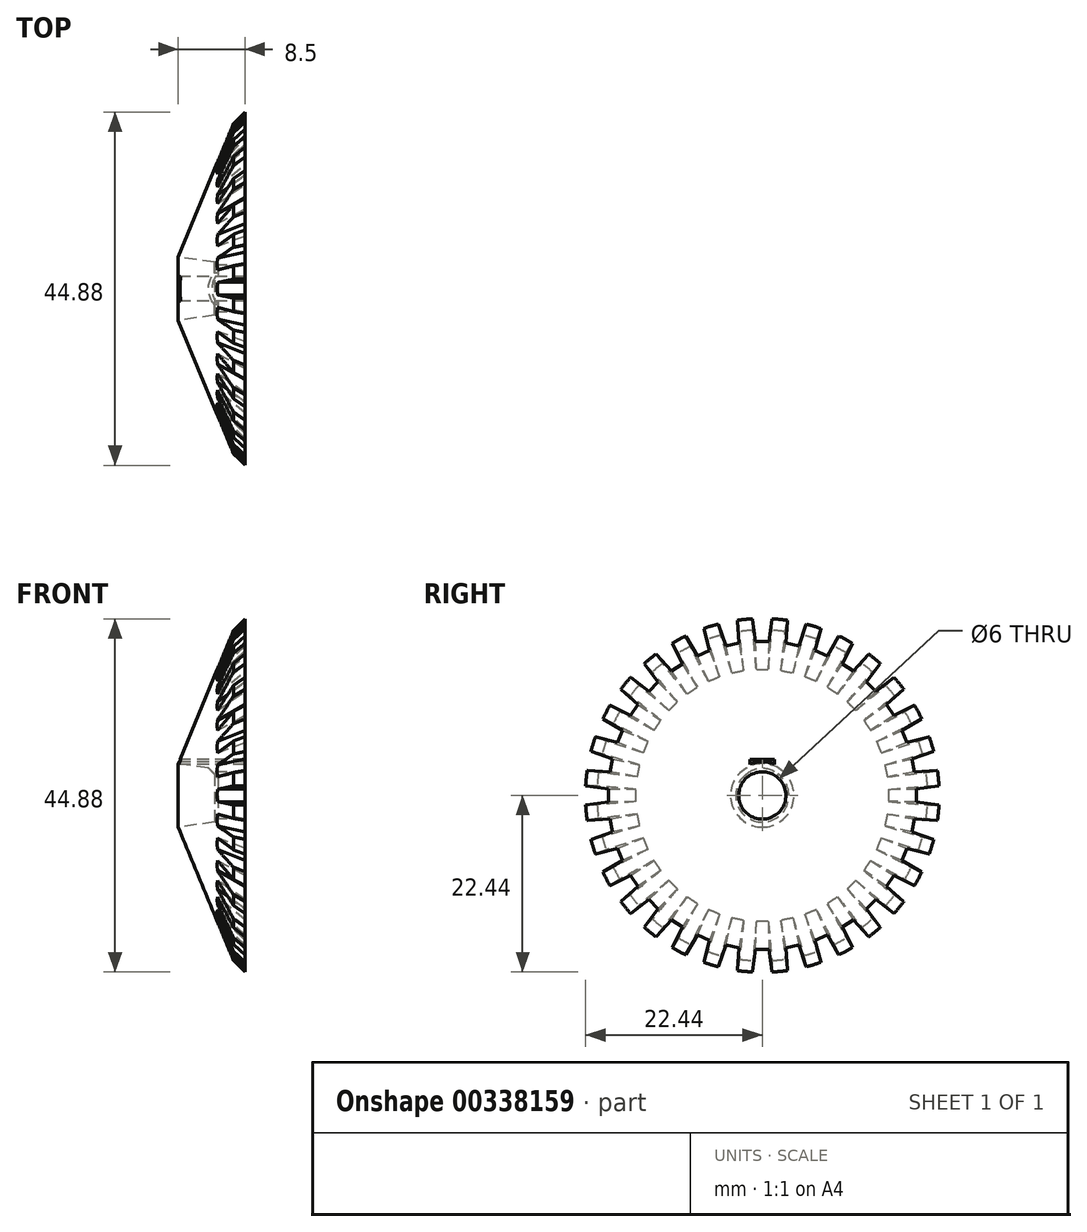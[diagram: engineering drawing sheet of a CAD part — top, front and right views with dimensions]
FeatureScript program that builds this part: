
annotation { "Feature Type Name" : "Feature", "Feature Type Description" : "" }
export const myFeature = defineFeature(function(context is Context, id is Id, definition is map)
    precondition{}
    {
        {
            var Q0;
            Q0=qCreatedBy(makeId("Front.planeOp"),FACE);
            var sketch = newSketch(context, id + "F0", { "sketchPlane" : qUnion([Q0])});
            skLineSegment(sketch, "E0", {"start": v(0, 0) * mm, "end": v(35.34, 35.34) * mm});
            skLineSegment(sketch, "E1", {"start": v(0, 0) * mm, "end": v(38.3, 0) * mm});
            skLineSegment(sketch, "E2", {"start": v(0, 0) * mm, "end": v(-10.6, 10.6) * mm});
            skLineSegment(sketch, "E3", {"start": v(-10.6, 10.6) * mm, "end": v(24.73, 45.94) * mm});
            skLineSegment(sketch, "E4", {"start": v(24.73, 45.94) * mm, "end": v(35.34, 35.34) * mm});
            skSolve(sketch);
        }
        {
            var Q0;
            Q0=makeQuery(id+"F0.imprint","IMPRINT",FACE,{"disambiguationData":[TD([[makeQuery(id+"F0.imprint","IMPRINT",EDGE,{"derivedFrom":sQuery(id+"F0.wireOp",EDGE,"E0")}),1.0]])]});
            extrude(context, id + "F1", {"entities" : qUnion([Q0]), "endBound" : BoundingType.SYMMETRIC, "depth" : 4 * mm});
        }
        {
            var Q0;
            Q0=makeQuery(id+"F1.opExtrude","SWEPT_FACE",FACE,{"disambiguationData":[OSD([sQuery(id+"F0.wireOp",EDGE,"E3")])]});
            var sketch = newSketch(context, id + "F2", { "sketchPlane" : qUnion([Q0])});
            skPoint(sketch, "E5", {"position": v(-2, 49.97) * mm});
            skPoint(sketch, "E6", {"position": v(-1, -0.02) * mm});
            skLineSegment(sketch, "E7", {"start": v(-1, -0.02) * mm, "end": v(1, 0.02) * mm, "construction": true});
            skPoint(sketch, "E8", {"position": v(0, 0) * mm});
            skLineSegment(sketch, "E9", {"start": v(0, -8) * mm, "end": v(0, -12.28) * mm, "construction": true});
            skLineSegment(sketch, "E10", {"start": v(1.74, 52.97) * mm, "end": v(-1.74, 52.97) * mm});
            skLineSegment(sketch, "E11", {"start": v(0.94, -3.02) * mm, "end": v(-0.94, -3.02) * mm});
            skLineSegment(sketch, "E12", {"start": v(-0.94, -3.02) * mm, "end": v(-1.74, 52.97) * mm});
            skLineSegment(sketch, "E13.MirrorCS", {"start": v(0.94, -3.02) * mm, "end": v(1.74, 52.97) * mm});
            skSolve(sketch);
        }
        {
            var Q0;
            Q0=qCreatedBy(makeId("Top.planeOp"),FACE);
            var sketch = newSketch(context, id + "F3", { "sketchPlane" : qUnion([Q0])});
            skLineSegment(sketch, "E14", {"start": v(0, 0) * mm, "end": v(0, -17.72) * mm});
            skLineSegment(sketch, "E15", {"start": v(0, 0) * mm, "end": v(21.3, 0) * mm});
            skSolve(sketch);
        }
        {
            var Q0;
            Q0=makeQuery(id+"F1.opExtrude","CAP_FACE",FACE,{"disambiguationData":[OSD([sQuery(id+"F0.wireOp",EDGE,"E0"),sQuery(id+"F0.wireOp",EDGE,"E2"),sQuery(id+"F0.wireOp",EDGE,"E3"),sQuery(id+"F0.wireOp",EDGE,"E4")])],"isStart":false});
            var Q1;
            Q1=sQuery(id+"F3.wireOp",EDGE,"E15");
            revolve(context, id + "F4", {"operationType" : NewBodyOperationType.ADD, "entities" : qUnion([Q0]), "axis" : qUnion([Q1]), "revolveType" : RevolveType.FULL});
        }
        {
            var Q0;
            {var subQ0=sQuery(id+"F2.wireOp",EDGE,"E12");var subQ1=sQuery(id+"F0.wireOp",EDGE,"E3");var subQ2=makeQuery(id+"F1.opExtrude","SWEPT_EDGE",EDGE,{"disambiguationData":[OSD([sQuery(id+"F0.wireOp",EDGE,"E2"),subQ1])]});var subQ3=makeQuery(id+"F2.imprint","INTERSECT",VERTEX,{"derivedFrom":[subQ2,subQ0]});Q0=makeQuery(id+"F2.imprint","IMPRINT",FACE,{"disambiguationData":[TD([[makeQuery(id+"F2.imprint","IMPRINT",EDGE,{"disambiguationData":[TD([[subQ3,-1.0]])],"derivedFrom":subQ0}),-1.0]])]});}
            var Q1;
            {var subQ0=sQuery(id+"F2.wireOp",EDGE,"E11");Q1=makeQuery(id+"F2.imprint","IMPRINT",FACE,{"disambiguationData":[TD([[makeQuery(id+"F2.imprint","IMPRINT",EDGE,{"derivedFrom":subQ0}),-1.0]])]});}
            var Q2;
            {var subQ0=sQuery(id+"F2.wireOp",EDGE,"E10");Q2=makeQuery(id+"F2.imprint","IMPRINT",FACE,{"disambiguationData":[TD([[makeQuery(id+"F2.imprint","IMPRINT",EDGE,{"derivedFrom":subQ0}),1.0]])]});}
            extrude(context, id + "F5", {"entities" : qUnion([Q0, Q1, Q2]), "oppositeDirection" : true, "depth" : 2 * mm, "hasDraft" : true, "draftAngle" : 10 * degree, "draftPullDirection" : true, "hasSecondDirection" : true, "secondDirectionOppositeDirection" : false, "secondDirectionDepth" : 1 * mm});
        }
        {
            var Q0;
            Q0=makeQuery(id+"F5.opExtrude","SWEPT_BODY",BODY,{"disambiguationData":[OSD([sQuery(id+"F2.wireOp",EDGE,"E10"),sQuery(id+"F2.wireOp",EDGE,"E11"),sQuery(id+"F2.wireOp",EDGE,"E12"),sQuery(id+"F2.wireOp",EDGE,"E13.MirrorCS")])]});
            var Q1;
            Q1=sQuery(id+"F3.wireOp",EDGE,"E15");
            circularPattern(context, id + "F6", {"operationType" : NewBodyOperationType.REMOVE, "entities" : qUnion([Q0]), "axis" : qUnion([Q1]), "angle" : 360 * degree, "instanceCount" : 32, "equalSpace" : true});
        }
        {
            var Q0;
            Q0=qCreatedBy(makeId("Right.planeOp"),FACE);
            var sketch = newSketch(context, id + "F7", { "sketchPlane" : qUnion([Q0])});
            skCircle(sketch, "E16", {"center": v(0, 0) * mm, "radius": 35.4 * mm});
            skPoint(sketch, "E17", {"position": v(0, 45.94) * mm});
            skCircle(sketch, "E18", {"center": v(0, 0) * mm, "radius": 3 * mm});
            skSolve(sketch);
        }
        {
            var Q0;
            Q0=makeQuery(id+"F7.imprint","IMPRINT",FACE,{"disambiguationData":[TD([[makeQuery(id+"F7.imprint","IMPRINT",EDGE,{"derivedFrom":sQuery(id+"F7.wireOp",EDGE,"E16")}),1.0]])]});
            var Q1;
            Q1=sQuery(id+"F0.wireOp",VERTEX,"E4.end");
            extrude(context, id + "F8", {"entities" : qUnion([Q0]), "operationType" : NewBodyOperationType.ADD, "endBound" : BoundingType.UP_TO_VERTEX, "endBoundEntityVertex" : qUnion([Q1]), "depth" : 56.9 * mm, "hasSecondDirection" : true, "secondDirectionOppositeDirection" : false, "secondDirectionDepth" : 25.7 * mm});
        }
        {
            var Q0;
            Q0=qCreatedBy(makeId("Top.planeOp"),FACE);
            var sketch = newSketch(context, id + "F9", { "sketchPlane" : qUnion([Q0])});
            skLineSegment(sketch, "E19.bottom", {"start": v(26.17, 74.13) * mm, "end": v(56.17, 74.13) * mm});
            skLineSegment(sketch, "E19.top", {"start": v(26.17, -66.7) * mm, "end": v(56.17, -66.7) * mm});
            skLineSegment(sketch, "E19.left", {"start": v(26.17, 74.13) * mm, "end": v(26.17, -66.7) * mm});
            skLineSegment(sketch, "E19.right", {"start": v(56.17, 74.13) * mm, "end": v(56.17, -66.7) * mm});
            skSolve(sketch);
        }
        {
            var Q0;
            Q0=makeQuery(id+"F9.imprint","IMPRINT",FACE,{"disambiguationData":[TD([[makeQuery(id+"F9.imprint","IMPRINT",EDGE,{"derivedFrom":sQuery(id+"F9.wireOp",EDGE,"E19.bottom")}),-1.0]])]});
            extrude(context, id + "F10", {"entities" : qUnion([Q0]), "operationType" : NewBodyOperationType.REMOVE, "endBound" : BoundingType.SYMMETRIC, "oppositeDirection" : true, "depth" : 112 * mm});
        }
        {
            var Q0;
            Q0=qCreatedBy(makeId("Right.planeOp"),FACE);
            var sketch = newSketch(context, id + "F11", { "sketchPlane" : qUnion([Q0])});
            skCircle(sketch, "E20", {"center": v(0, 0) * mm, "radius": 10.6 * mm});
            skPoint(sketch, "E21", {"position": v(0, 10.6) * mm});
            skCircle(sketch, "E22", {"center": v(0, 0) * mm, "radius": 3 * mm});
            skLineSegment(sketch, "E23.bottom", {"start": v(1.56, 2.56) * mm, "end": v(-1.56, 2.56) * mm, "construction": true});
            skLineSegment(sketch, "E23.top", {"start": v(1.56, -1.18) * mm, "end": v(-1.56, -1.18) * mm});
            skLineSegment(sketch, "E23.left", {"start": v(1.56, 2.56) * mm, "end": v(1.56, -1.18) * mm});
            skLineSegment(sketch, "E23.right", {"start": v(-1.56, 2.56) * mm, "end": v(-1.56, -1.18) * mm});
            skPoint(sketch, "E24", {"position": v(0, 2.56) * mm});
            skLineSegment(sketch, "E25.top", {"start": v(1.56, 4.56) * mm, "end": v(-1.56, 4.56) * mm});
            skLineSegment(sketch, "E25.left", {"start": v(1.56, -1.18) * mm, "end": v(1.56, 4.56) * mm});
            skLineSegment(sketch, "E25.right", {"start": v(-1.56, -1.18) * mm, "end": v(-1.56, 4.56) * mm});
            skSolve(sketch);
        }
        {
            var Q0;
            Q0=makeQuery(id+"F11.imprint","IMPRINT",FACE,{"disambiguationData":[TD([[makeQuery(id+"F11.imprint","IMPRINT",EDGE,{"derivedFrom":sQuery(id+"F11.wireOp",EDGE,"E20")}),1.0]])]});
            var Q1;
            {var subQ5=sQuery(id+"F11.wireOp",EDGE,"E23.top");Q1=makeQuery(id+"F11.imprint","IMPRINT",FACE,{"disambiguationData":[TD([[makeQuery(id+"F11.imprint","IMPRINT",EDGE,{"derivedFrom":subQ5}),1.0]])]});}
            var Q2;
            {var subQ5=sQuery(id+"F11.wireOp",EDGE,"E23.top");Q2=makeQuery(id+"F11.imprint","IMPRINT",FACE,{"disambiguationData":[TD([[makeQuery(id+"F11.imprint","IMPRINT",EDGE,{"derivedFrom":subQ5}),-1.0]])]});}
            var Q3;
            {var subQ5=sQuery(id+"F11.wireOp",EDGE,"E25.top");Q3=makeQuery(id+"F11.imprint","IMPRINT",FACE,{"disambiguationData":[TD([[makeQuery(id+"F11.imprint","IMPRINT",EDGE,{"derivedFrom":subQ5}),1.0]])]});}
            extrude(context, id + "F12", {"entities" : qUnion([Q0, Q1, Q2, Q3]), "operationType" : NewBodyOperationType.ADD, "oppositeDirection" : true, "depth" : 9 * mm, "hasDraft" : true, "draftAngle" : 8 * degree, "draftPullDirection" : true});
        }
        {
            var Q0;
            Q0=makeQuery(id+"F12.opExtrude","CAP_FACE",FACE,{"disambiguationData":[OSD([sQuery(id+"F11.wireOp",EDGE,"E20")])],"isStart":false});
            var sketch = newSketch(context, id + "F13", { "sketchPlane" : qUnion([Q0])});
            skCircle(sketch, "E26", {"center": v(0, 0) * mm, "radius": 3 * mm});
            skLineSegment(sketch, "E27.bottom", {"start": v(-1.56, 4.56) * mm, "end": v(1.56, 4.56) * mm});
            skLineSegment(sketch, "E27.top", {"start": v(-1.56, 2) * mm, "end": v(1.56, 2) * mm, "construction": true});
            skLineSegment(sketch, "E27.left", {"start": v(-1.56, 4.56) * mm, "end": v(-1.56, 2) * mm});
            skLineSegment(sketch, "E27.right", {"start": v(1.56, 4.56) * mm, "end": v(1.56, 2) * mm});
            skSolve(sketch);
        }
        {
            var Q0;
            Q0=makeQuery(id+"F10.boolean.opBoolean","COPY",FACE,{"derivedFrom":makeQuery(id+"F10.opExtrude","SWEPT_FACE",FACE,{"disambiguationData":[OSD([sQuery(id+"F9.wireOp",EDGE,"E19.left")])]})});
            var sketch = newSketch(context, id + "F14", { "sketchPlane" : qUnion([Q0])});
            skCircle(sketch, "E28", {"center": v(0, 0) * mm, "radius": 3 * mm});
            skSolve(sketch);
        }
        {
            var Q0;
            Q0=makeQuery(id+"F14.imprint","IMPRINT",FACE,{"disambiguationData":[TD([[makeQuery(id+"F14.imprint","IMPRINT",EDGE,{"derivedFrom":sQuery(id+"F14.wireOp",EDGE,"E28")}),-1.0]])]});
            var Q1;
            Q1=sQuery(id+"F11.wireOp",VERTEX,"E21");
            extrude(context, id + "F15", {"entities" : qUnion([Q0]), "operationType" : NewBodyOperationType.ADD, "endBound" : BoundingType.UP_TO_VERTEX, "oppositeDirection" : true, "endBoundEntityVertex" : qUnion([Q1]), "depth" : 25 * mm, "hasDraft" : true, "draftAngle" : 3 * degree});
        }
        {
            var Q0;
            {var subQ5=sQuery(id+"F13.wireOp",EDGE,"E27.bottom");Q0=makeQuery(id+"F13.imprint","IMPRINT",FACE,{"disambiguationData":[TD([[makeQuery(id+"F13.imprint","IMPRINT",EDGE,{"derivedFrom":subQ5}),-1.0]])]});}
            var Q1;
            {var subQ0=sQuery(id+"F13.wireOp",EDGE,"E26");var subQ1=makeQuery(id+"F13.imprint","INTERSECT",VERTEX,{"derivedFrom":[subQ0,sQuery(id+"F13.wireOp",EDGE,"E27.left")]});Q1=makeQuery(id+"F13.imprint","IMPRINT",FACE,{"disambiguationData":[TD([[makeQuery(id+"F13.imprint","IMPRINT",EDGE,{"disambiguationData":[TD([[subQ1,1.0]])],"derivedFrom":subQ0}),1.0]])]});}
            extrude(context, id + "F16", {"entities" : qUnion([Q0, Q1]), "operationType" : NewBodyOperationType.REMOVE, "oppositeDirection" : true, "depth" : 288.6 * mm});
        }
        {
            var Q0;
            Q0=makeQuery(id+"F15.boolean.opBoolean","MERGE",FACE,{"derivedFrom":[makeQuery(id+"F10.boolean.opBoolean","COPY",FACE,{"derivedFrom":makeQuery(id+"F10.opExtrude","SWEPT_FACE",FACE,{"disambiguationData":[OSD([sQuery(id+"F9.wireOp",EDGE,"E19.left")])]})}),makeQuery(id+"F15.opExtrude","CAP_FACE",FACE,{"disambiguationData":[OSD([sQuery(id+"F14.wireOp",EDGE,"E28")])],"isStart":true})]});
            var sketch = newSketch(context, id + "F17", { "sketchPlane" : qUnion([Q0])});
            skLineSegment(sketch, "E29.bottom", {"start": v(-85.01, 76.56) * mm, "end": v(100.06, 76.56) * mm});
            skLineSegment(sketch, "E29.top", {"start": v(-85.01, -83.72) * mm, "end": v(100.06, -83.72) * mm});
            skLineSegment(sketch, "E29.left", {"start": v(-85.01, 76.56) * mm, "end": v(-85.01, -83.72) * mm});
            skLineSegment(sketch, "E29.right", {"start": v(100.06, 76.56) * mm, "end": v(100.06, -83.72) * mm});
            skSolve(sketch);
        }
        {
            var Q0;
            Q0=makeQuery(id+"F17.imprint","IMPRINT",FACE,{"disambiguationData":[TD([[makeQuery(id+"F17.imprint","IMPRINT",EDGE,{"derivedFrom":sQuery(id+"F17.wireOp",EDGE,"E29.bottom")}),-1.0]])]});
            var Q1;
            {var subQ0=makeQuery(id+"F10.opExtrude","SWEPT_FACE",FACE,{"disambiguationData":[OSD([sQuery(id+"F9.wireOp",EDGE,"E19.left")])]});var subQ1=makeQuery(id+"F4.opRevolve","SWEPT_FACE",FACE,{"disambiguationData":[OSD([sQuery(id+"F0.wireOp",EDGE,"E4")])]});Q1=makeQuery(id+"F17.imprint","IMPRINT",FACE,{"disambiguationData":[TD([[makeQuery(id+"F17.imprint","IMPRINT",EDGE,{"derivedFrom":makeQuery(id+"F10.boolean.opBoolean","INTERSECT",EDGE,{"disambiguationData":[OD(0.0)],"derivedFrom":[subQ1,subQ0]})}),1.0]])]});}
            extrude(context, id + "F18", {"entities" : qUnion([Q0, Q1]), "operationType" : NewBodyOperationType.REMOVE, "oppositeDirection" : true, "depth" : 25 * mm});
        }
        {
            var Q0;
            Q0=qCreatedBy(makeId("Front.planeOp"),FACE);
            var sketch = newSketch(context, id + "F19", { "sketchPlane" : qUnion([Q0])});
            skLineSegment(sketch, "E30", {"start": v(-9, 0) * mm, "end": v(2.1, 26.8) * mm});
            skLineSegment(sketch, "E31", {"start": v(2.1, 26.8) * mm, "end": v(-9, 26.8) * mm});
            skLineSegment(sketch, "E32", {"start": v(-9, 0) * mm, "end": v(-42.06, 0) * mm, "construction": true});
            skLineSegment(sketch, "E33", {"start": v(-9, 26.8) * mm, "end": v(-20.1, 0) * mm});
            skLineSegment(sketch, "E34", {"start": v(-20.1, 0) * mm, "end": v(-9, 0) * mm});
            skSolve(sketch);
        }
        {
            var Q0;
            Q0=makeQuery(id+"F19.imprint","IMPRINT",FACE,{"disambiguationData":[TD([[makeQuery(id+"F19.imprint","IMPRINT",EDGE,{"derivedFrom":sQuery(id+"F19.wireOp",EDGE,"E30")}),1.0]])]});
            var Q1;
            Q1=sQuery(id+"F19.wireOp",EDGE,"E34");
            revolve(context, id + "F20", {"operationType" : NewBodyOperationType.REMOVE, "entities" : qUnion([Q0]), "axis" : qUnion([Q1]), "revolveType" : RevolveType.FULL, "oppositeDirection" : true});
        }
    });
